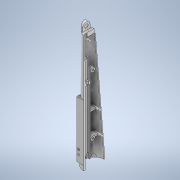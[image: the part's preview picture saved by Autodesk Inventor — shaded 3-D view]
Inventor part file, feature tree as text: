
AUTODESK INVENTOR PART (.ipt)
format: ipt  version: 2021 (Build 250183000, 183)  size: 1,118,720 bytes
history: native  units: mm
features: sketch x40, extrude x37, plane x17, fillet x7, hole x3, thread x3, loft x2, revolve x2, other x1
ambient origin geometry x8: Origin, YZ Plane, XZ Plane, XY Plane, X Axis, Y Axis, Z Axis, Center Point
bodies: Body1 (feature_tree)
feature tree (112):
  other  "Sólido1"
  plane  "Plano de trabajo1"
  plane  "Plano de trabajo2"
  plane  "Plano de trabajo4"
  plane  "Plano de trabajo5"
  plane  "Plano de trabajo6"
  sketch  "Boceto1"  dims[d1=250.0mm d2=0.0mm d3=-80.0mm d4=-110.0mm]
  sketch  "Boceto2"  dims[d5=-140.0mm d7=-0.0mm d8=2.0mm]
  sketch  "Boceto3"  dims[d9=140.0mm d10=250.0mm]
  sketch  "Boceto4"  dims[d11=24.0mm d22=0.0mm d23=90.0deg d24=0.0mm d25=90.0deg]
  sketch  "Boceto6"  dims[d44=45.0mm d49=29.11157mm]
  sketch  "Boceto7"  dims[d50=29.11157mm d53=29.11157mm]
  loft  "Solevación1"
  fillet  "Empalme2"  [1 undecoded]
  extrude  "Extrusión1"  TaperAngle=0.0deg  [1 undecoded]
  fillet  "Empalme5"  Radius=2.0mm
  plane  "Plano de trabajo7"
  extrude  "Extrusión2"  Depth=250.0mm
  plane  "Plano de trabajo8"
  plane  "Plano de trabajo9"
  loft  "Solevación9"
  plane  "Plano de trabajo10"
  extrude  "Extrusión3"  Depth=29.11157mm
  plane  "Plano de trabajo11"
  revolve  "Revolución1"  [1 undecoded]
  revolve  "Revolución2"  [1 undecoded]
  extrude  "Extrusión4"  Depth=32.5mm
  plane  "Plano de trabajo12"
  extrude  "Extrusión5"  Depth=44.747934mm
  plane  "Plano de trabajo13"
  plane  "Plano de trabajo14"
  extrude  "Extrusión6"  Depth=42.747934mm
  extrude  "Extrusión7"  Depth=42.747934mm
  extrude  "Extrusión8"  Depth=13.0mm
  extrude  "Extrusión11"  Depth=7.75mm
  extrude  "Extrusión9"  Depth=7.75mm
  extrude  "Extrusión10"  Depth=16.0mm
  extrude  "Extrusión12"  Depth=12.0mm
  sketch  "Boceto30"  dims[d160=-19.75mm d161=0.0mm]
  extrude  "Extrusión13"  Depth=7.75mm
  extrude  "Extrusión14"  Depth=7.75mm
  extrude  "Extrusión15"  TaperAngle=0.0deg  [1 undecoded]
  hole  "Agujero1"  [1 undecoded]
  thread  "Rosca1"  [1 undecoded]
  extrude  "Extrusión16"  Depth=2.0mm
  plane  "Plano de trabajo16"
  extrude  "Extrusión17"  TaperAngle=0.0deg  [1 undecoded]
  extrude  "Extrusión18"  TaperAngle=0.0deg  [1 undecoded]
  plane  "Plano de trabajo17"
  sketch  "Boceto46"  dims[d185=2.0mm d187=1.0mm]
  hole  "Agujero2"  [1 undecoded]
  hole  "Agujero3"  [1 undecoded]
  plane  "Plano de trabajo19"
  sketch  "Boceto50"  dims[d193=0.25mm d194=90.0deg d196=4.381635mm d197=0.0mm]
  extrude  "Extrusión22"  Depth=12.0mm
  extrude  "Extrusión23"  [1 undecoded]
  extrude  "Extrusión24"  Depth=0.75mm
  plane  "Plano de trabajo20"
  extrude  "Extrusión25"  Depth=1.0mm
  fillet  "Empalme6"  Radius=11.0mm
  fillet  "Empalme7"  Radius=17.453293mm
  sketch  "Boceto49"  dims[d191=2.0mm d192=0.25mm]
  extrude  "Extrusión29"  Depth=0.75mm
  extrude  "Extrusión30"  Depth=0.25mm
  sketch  "Boceto44"  dims[d181=0.75mm d182=0.25mm]
  sketch  "Boceto47"  dims[d189=3.0mm d190=2.0mm]
  extrude  "Extrusión26"  Depth=0.25mm
  extrude  "Extrusión27"  Depth=1.0mm
  extrude  "Extrusión28"  Depth=2.0mm
  sketch  "Boceto45"  dims[d183=1.0mm d184=0.25mm]
  extrude  "Extrusión31"  Depth=0.25mm
  extrude  "Extrusión32"  TaperAngle=90.0deg  [1 undecoded]
  fillet  "Empalme8"  Radius=4.381635mm
  extrude  "Extrusión33"  Depth=12.0mm
  extrude  "Extrusión34"  Depth=9.0mm
  thread  "Rosca2"  [1 undecoded]
  thread  "Rosca3"  [1 undecoded]
  fillet  "Empalme9"  Radius=201.65mm
  extrude  "Extrusión35"  Depth=0.5mm
  extrude  "Extrusión36"  [1 undecoded]
  sketch  "Boceto53"  dims[d205=0.0mm d206=0.5mm]
  extrude  "Agujero_tornillo_caja"  Depth=100.0mm TaperAngle=0.0deg
  extrude  "Extrusión39"  Depth=35.0mm TaperAngle=0.0deg
  extrude  "Test_section"  Depth=210.0mm TaperAngle=0.0deg
  extrude  "Agujero_cables"  Depth=2.0mm
  fillet  "Empalme10"  Radius=1.059493mm
  sketch  "Boceto9"  dims[d59=29.11157mm d61=29.11157mm]
  sketch  "Boceto10"  dims[d65=22.5mm d66=32.5mm]
  sketch  "Boceto15"  dims[d67=22.5mm d90=44.747934mm]
  sketch  "Boceto16"  dims[d91=42.747934mm d93=42.747934mm]
  sketch  "Boceto17"  dims[d96=0.0mm d97=90.0deg d98=0.0mm d99=90.0deg d100=0.0mm d101=90.0deg d102=0.0mm d103=90.0deg d112=42.747934mm]
  sketch  "Boceto18"  dims[d115=5.0mm d120=13.0mm]
  sketch  "Boceto19"  dims[d121=6.5mm d124=7.75mm]
  sketch  "Boceto20"  dims[d125=7.75mm d126=7.75mm]
  sketch  "Boceto21"  dims[d127=7.75mm d130=16.0mm]
  sketch  "Boceto22"  dims[d131=0.0mm d132=12.0mm]
  sketch  "Boceto24"  dims[d133=12.0mm d134=7.75mm]
  sketch  "Boceto25"  dims[d135=6.5mm d136=7.75mm]
  sketch  "Boceto26"  dims[d137=15.0mm d138=0.0mm]
  sketch  "Boceto27"  dims[d146=-8.5mm d147=30.0mm d148=2.0mm]
  sketch  "Boceto28"  dims[d149=25.12mm d150=2.0mm]
  sketch  "Boceto29"  dims[d151=10.357mm d156=0.0mm d157=90.0deg d158=0.0mm d159=90.0deg]
  sketch  "Boceto31"  dims[d163=0.0mm d164=2.0mm]
  sketch  "Boceto36"  dims[d165=15.0mm d166=4.0mm]
  sketch  "Boceto37"  dims[d167=30.0mm d168=12.0mm]
  sketch  "Boceto38"  dims[d169=0.0mm d170=-7.25mm]
  sketch  "Boceto39"  dims[d171=4.5mm d172=0.75mm]
  sketch  "Boceto40"  dims[d173=2.5mm d174=1.0mm d176=11.0mm d177=17.453293mm]
  sketch  "Boceto41"  dims[d179=2.939597mm d180=0.75mm]
  sketch  "Boceto51"  dims[d198=-48.35mm d199=12.0mm]
  sketch  "Boceto52"  dims[d200=20.0mm d201=9.0mm d202=9.0mm d203=2.0mm d204=201.65mm]
  sketch  "Boceto54"  dims[d207=0.25mm d208=-7.5mm d209=100.0mm d210=0.0mm d211=35.0mm d212=0.0mm d213=210.0mm d214=0.0mm d215=2.0mm d216=1.059493mm d217=6.5mm d218=1.059493mm d219=5.0mm d220=2.0mm d221=0.0mm d222=2.0mm d223=6.5mm d224=1.059493mm d225=5.0mm d226=4.85mm d227=2.0mm d228=0.0mm d229=6.0mm d230=10.0mm d231=3.0mm d232=11.0mm d233=10.5mm d235=30.0deg d236=4.75mm d237=0.0mm d238=-17.0mm d239=100.0mm d240=0.0mm d241=6.5mm d242=1.65mm d243=3.3mm d244=15.6mm d245=2.0mm d247=16.0mm d248=2.0mm d249=0.0mm d250=4.5mm d251=0.75mm d252=2.5mm d253=1.0mm d254=11.0mm d255=17.453293mm d256=2.939597mm d257=0.75mm d258=0.75mm d259=0.25mm d260=1.0mm d261=0.25mm d262=2.0mm d263=1.0mm d264=3.0mm d265=2.0mm d266=2.0mm d267=0.25mm d268=0.25mm d269=40.0mm d270=1.0mm d271=1.0mm d272=7.75mm d273=0.5mm d274=8.5mm d275=90.0deg d276=0.0mm d277=17.75mm d280=22.5mm d281=2.0mm d282=0.0mm d283=0.0mm d292=2.0mm d293=0.0mm d296=3.5mm d297=0.0mm d299=4.0mm d300=3.708mm d301=3.023mm d302=2.0mm d303=14.3117mm d304=16.0mm d305=0.0mm d306=16.0mm d307=0.0mm d314=6.0mm d315=19.2mm d316=6.0mm d317=19.2mm d318=13.0mm d320=6.0mm d321=19.2mm d322=13.0mm d323=6.0mm d324=19.2mm d325=13.0mm d326=7.0mm d332=10.0mm d333=0.0mm d335=-41.6mm d336=4.0mm d337=1.0mm d338=9.0mm d339=4.0mm d340=1.0mm d341=9.0mm d342=4.0mm d343=5.2mm d344=6.0mm d345=0.0mm d346=15.0mm d347=5.0mm d349=5.0mm d351=0.0mm d352=45.0mm d354=10.0mm d355=10.0mm d356=0.0mm d357=15.0mm d358=0.0mm d359=2.0mm d363=50.4125mm d376=14.059493mm d377=2.0mm d378=0.0mm d379=2.0mm d380=11.25mm d381=90.0mm d382=290.0mm d383=14.059493mm d384=100.825mm d390=30.940507mm d391=2.0mm d392=100.825mm d393=14.790546mm d394=2.0mm d395=3.0mm d396=4.0mm d397=4.0mm d398=4.0mm d399=4.0mm d400=8.128453mm d401=12.0mm d402=4.45mm d403=2.5mm d404=1.65mm d405=1.65mm d406=1.0mm d407=2.0mm d408=2.0mm d409=0.0mm d411=50.4125mm d412=4.0mm d418=13.059493mm d419=6.5mm d420=6.5mm d421=50.4125mm d422=126.03125mm d423=0.0mm d424=15.0mm d425=5.0mm d426=5.0mm d427=0.0mm d428=45.0mm d429=10.0mm d430=2.0mm d431=4.0mm d432=6.0mm d433=8.0mm d434=2.0mm d435=90.0deg d436=20.0mm d437=0.0mm d438=4.0mm d439=6.0mm d440=8.0mm d441=2.0mm d442=90.0deg d443=20.0mm d444=0.0mm d447=2.0mm d448=11.5mm d450=4.0mm d451=4.0mm d452=90.0mm d453=750.0mm d454=22.5mm d455=43.0mm d456=44.0mm d457=14.059493mm d458=11.25mm d461=22.5mm d462=43.0mm d463=7.059493mm d464=3.0mm d465=6.0mm d466=3.0mm d467=6.0mm d468=45.0mm d469=130.0mm d470=17.04mm d471=30.0mm d472=15.0mm d473=0.0mm d474=1.5mm d475=2.0mm d476=1.5mm d477=2.0mm d478=120.0mm d479=0.0mm d480=120.0mm d481=0.0mm d482=116.0mm d483=0.0mm d484=69.0mm d485=0.0mm d486=-1.5mm d487=65.395511mm d488=2.6mm d489=60.0deg d490=45.0deg d491=15.0mm d492=1.6mm d493=0.0mm d494=180.0mm d495=0.0mm d496=180.0mm d497=0.0mm d498=2.0mm d499=0.0mm d500=4.4mm d501=4.1mm d502=10.0mm d503=0.0mm d504=7.0mm d505=0.0mm d506=9.0mm d507=9.0mm d508=0.0mm d509=0.0mm d510=6.0mm d511=0.0mm d512=2.0mm d513=0.0mm d514=0.0mm d515=10.0mm d516=0.0mm d517=10.0mm d518=0.0mm d519=10.0mm d520=0.0mm d521=1.0mm d522=1.0mm d523=6.5mm d524=9.0mm d525=3.0mm d526=1.5mm d527=3.0mm d528=1.5mm d529=0.0mm d530=0.0mm d531=3.0mm d532=2.4mm d533=0.0mm d534=135.0mm d535=4.0mm d536=130.0mm d537=0.0mm d538=0.0mm d539=25.0mm d540=11.0mm d541=4.0mm d542=6.0mm d543=12.0mm d544=0.0mm d545=10.0mm d546=0.0mm d547=10.0mm d548=22.5mm d549=4.0mm d550=9.0mm d551=4.0mm d552=1.0mm d553=10.0mm d554=0.0mm d555=2.0mm d556=13.0mm]
note: 16 required parameter values undecoded (feature->parameter linkage not recoverable at this tier; creation-order binding heuristic only, values carry confidence <= 0.55)